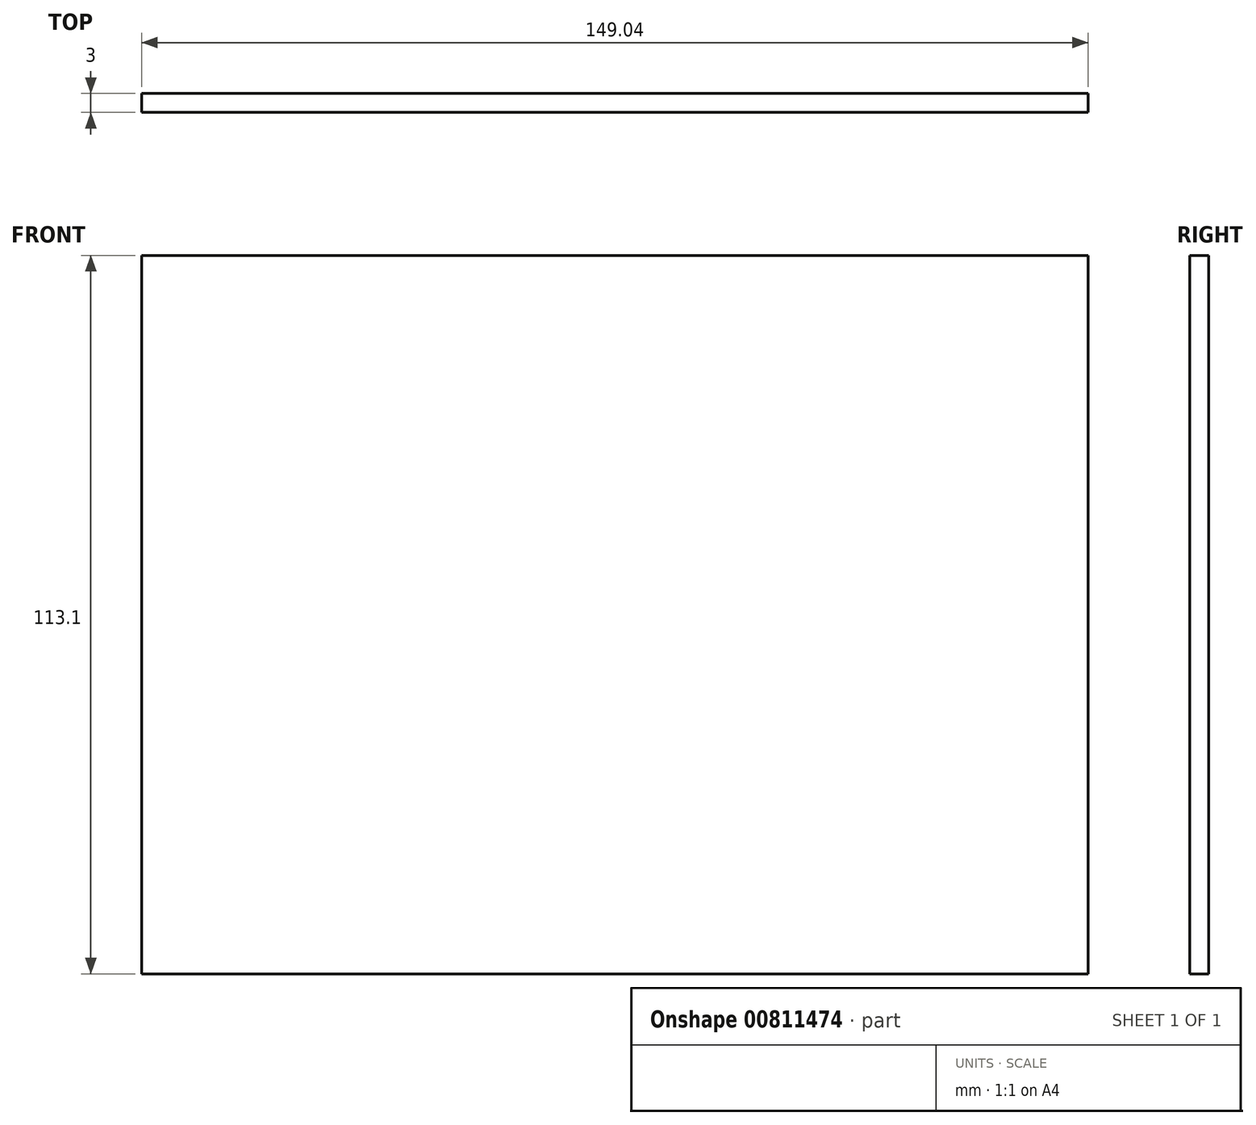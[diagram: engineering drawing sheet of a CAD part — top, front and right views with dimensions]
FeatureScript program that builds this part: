
annotation { "Feature Type Name" : "Feature", "Feature Type Description" : "" }
export const myFeature = defineFeature(function(context is Context, id is Id, definition is map)
    precondition{}
    {
        {
            var Q0;
            Q0=qCreatedBy(makeId("Front.planeOp"),FACE);
            var sketch = newSketch(context, id + "F0", { "sketchPlane" : qUnion([Q0])});
            skLineSegment(sketch, "E0.bottom", {"start": v(-74.39, 56.42) * mm, "end": v(74.65, 56.42) * mm});
            skLineSegment(sketch, "E0.top", {"start": v(-74.39, -56.68) * mm, "end": v(74.65, -56.68) * mm});
            skLineSegment(sketch, "E0.left", {"start": v(-74.39, 56.42) * mm, "end": v(-74.39, -56.68) * mm});
            skLineSegment(sketch, "E0.right", {"start": v(74.65, 56.42) * mm, "end": v(74.65, -56.68) * mm});
            skSolve(sketch);
        }
        {
            var Q0;
            Q0=makeQuery(id+"F0.imprint","IMPRINT",FACE,{"disambiguationData":[TD([[makeQuery(id+"F0.imprint","IMPRINT",EDGE,{"derivedFrom":sQuery(id+"F0.wireOp",EDGE,"E0.bottom")}),-1.0]])]});
            extrude(context, id + "F1", {"entities" : qUnion([Q0]), "depth" : 3 * mm, "offsetDistance" : 25 * mm});
        }
    });
